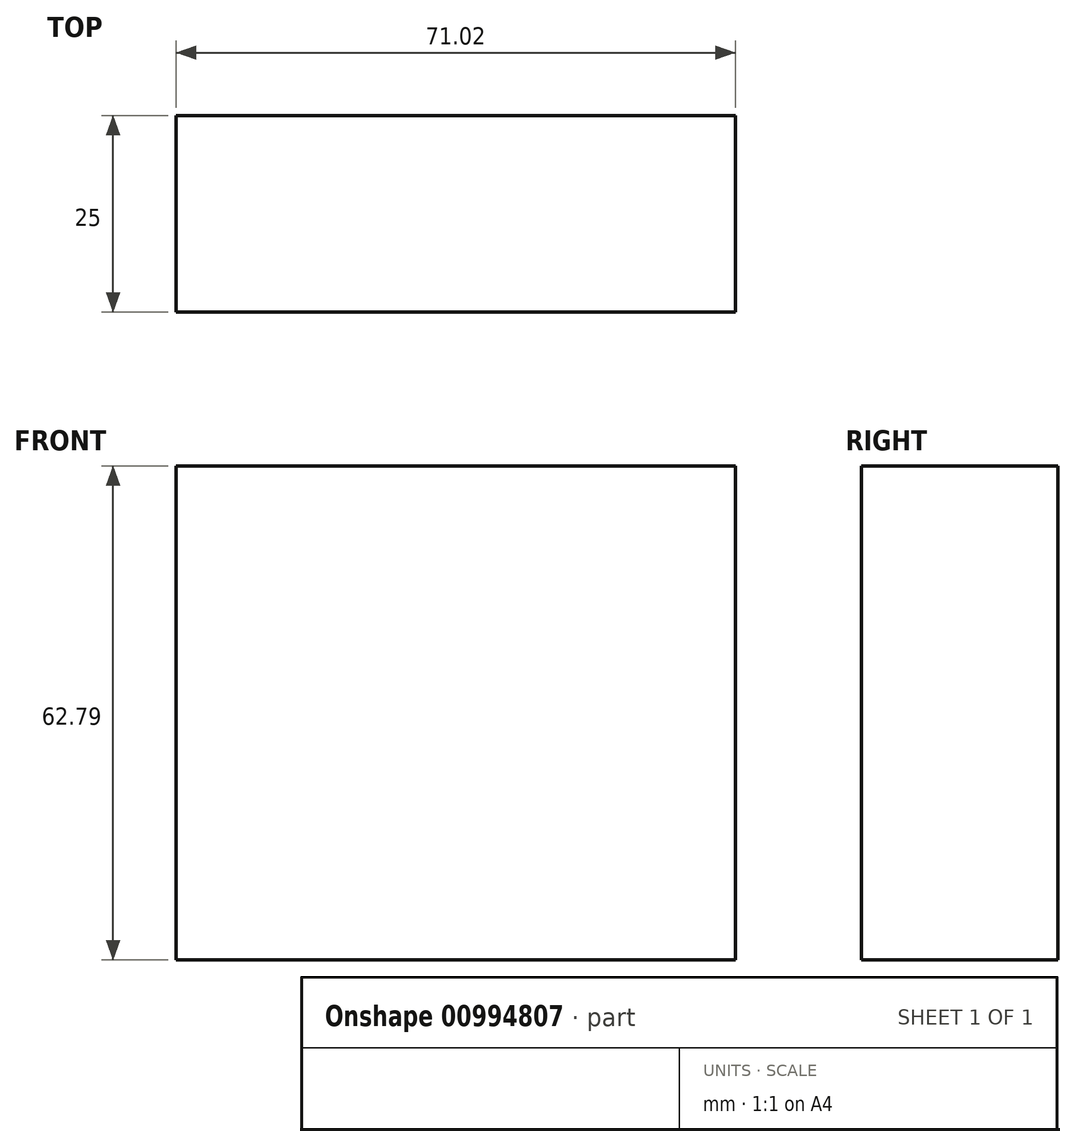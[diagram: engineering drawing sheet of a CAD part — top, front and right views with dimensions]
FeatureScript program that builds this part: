
annotation { "Feature Type Name" : "Feature", "Feature Type Description" : "" }
export const myFeature = defineFeature(function(context is Context, id is Id, definition is map)
    precondition{}
    {
        {
            var Q0;
            Q0=qCreatedBy(makeId("Front.planeOp"),FACE);
            var sketch = newSketch(context, id + "F0", { "sketchPlane" : qUnion([Q0])});
            skLineSegment(sketch, "E0.bottom", {"start": v(-148.02, 32.23) * mm, "end": v(-77, 32.23) * mm});
            skLineSegment(sketch, "E0.top", {"start": v(-148.02, -30.56) * mm, "end": v(-77, -30.56) * mm});
            skLineSegment(sketch, "E0.left", {"start": v(-148.02, 32.23) * mm, "end": v(-148.02, -30.56) * mm});
            skLineSegment(sketch, "E0.right", {"start": v(-77, 32.23) * mm, "end": v(-77, -30.56) * mm});
            skSolve(sketch);
        }
        {
            var Q0;
            Q0 = qSketchRegion(id + "F0", true);
            extrude(context, id + "F1", {"entities" : qUnion([Q0]), "depth" : 25 * mm, "offsetDistance" : 25 * mm});
        }
    });
